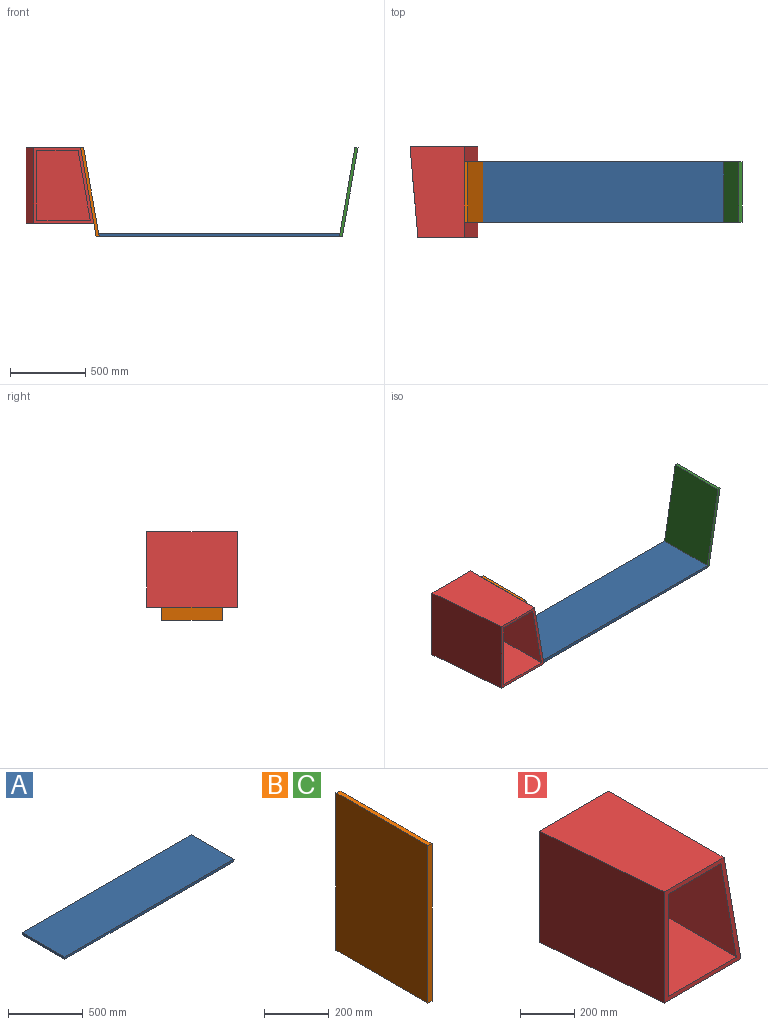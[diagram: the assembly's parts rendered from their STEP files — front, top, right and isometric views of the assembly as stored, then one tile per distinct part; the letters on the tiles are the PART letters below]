
ASSEMBLY  parts=4 mates=3
PART A: 6 faces, bbox 1600x400x20 mm
  f0: plane 1592.95x400mm, normal (0,0,-1), area 637178.8mm2, adj f2,f3,f4,f5
  f1: plane 1600x400mm, normal (0,0,1), area 640000mm2, adj f2,f3,f4,f5
  f2: plane 1600x20mm, normal (0,-1,0), area 31929.5mm2, adj f0,f1,f4,f5
  f3: plane 1600x20mm, normal (0,1,0), area 31929.5mm2, adj f0,f1,f4,f5
  f4: plane 400x20mm, normal (-0.98,0,-0.17), area 8123.4mm2, adj f0,f1,f2,f3
  f5: plane 400x20mm, normal (0.98,0,-0.17), area 8123.4mm2, adj f0,f1,f2,f3
PART B: 6 faces, bbox 20x400x600 mm
  f0: plane 596.47x400mm, normal (1,0,0), area 238589.4mm2, adj f2,f3,f4,f5
  f1: plane 596.47x400mm, normal (-1,0,0), area 238589.4mm2, adj f2,f3,f4,f5
  f2: plane 600x20mm, normal (0,-1,0), area 11929.5mm2, adj f0,f1,f4,f5
  f3: plane 600x20mm, normal (0,1,0), area 11929.5mm2, adj f0,f1,f4,f5
  f4: plane 400x20mm, normal (-0.17,0,-0.98), area 8123.4mm2, adj f0,f1,f2,f3
  f5: plane 400x20mm, normal (0.17,0,0.98), area 8123.4mm2, adj f0,f1,f2,f3
PART C: same geometry as B
PART D: 11 faces, bbox 450x600x500 mm
  f0: plane 500x397.51mm, normal (0,-1,0), area 32493mm2, adj f1,f2,f4,f5,f6,f7,f8,f9
  f1: plane 600x450mm, normal (0,0,-1), area 254252mm2, adj f0,f3,f4,f5
  f2: plane 600x361.84mm, normal (0,0,1), area 201353.9mm2, adj f0,f3,f4,f5
  f3: plane 500x450mm, normal (0,1,0), area 202959.1mm2, adj f1,f2,f4,f5
  f4: plane 600x500mm, normal (0.98,0,0.17), area 304628mm2, adj f0,f1,f2,f3
  f5: plane 600x500mm, normal (-1,-0.09,0), area 301146mm2, adj f0,f1,f2,f3
  f6: plane 580x460.48mm, normal (1,0,0), area 267076.5mm2, adj f0,f7,f9,f10
  f7: plane 580x353.59mm, normal (0,0,1), area 205080.6mm2, adj f0,f6,f8,f10
  f8: plane 580x460.36mm, normal (-0.98,0,-0.17), area 271083.7mm2, adj f0,f7,f9,f10
  f9: plane 580x272.87mm, normal (0,0,-1), area 158265.8mm2, adj f0,f6,f8,f10
  f10: plane 460.48x353.59mm, normal (0,-1,0), area 144219.5mm2, adj f6,f7,f8,f9
PLACE A t=(100.25,-39.18,98.66)mm
PLACE B rot(axis=(0,-1,0),10deg) t=(-1496.22,-39.18,98.66)mm
PLACE C rot(axis=(1,0,-0.09),180deg) t=(220.61,-439.18,686.07)mm
PLACE D t=(-1531.94,60.82,186.07)mm
MATE fastened B.f1 <-> D.f4  axis (-0.98,0,-0.17) through (-1620.1,-239.18,686.07)mm
MATE fastened A.f4 <-> B.f0  axis (-0.98,0,-0.17) through (-1496.22,-439.18,98.66)mm
MATE fastened A.f5 <-> C.f1  axis (0.98,0,-0.17) through (96.73,-439.18,98.66)mm
